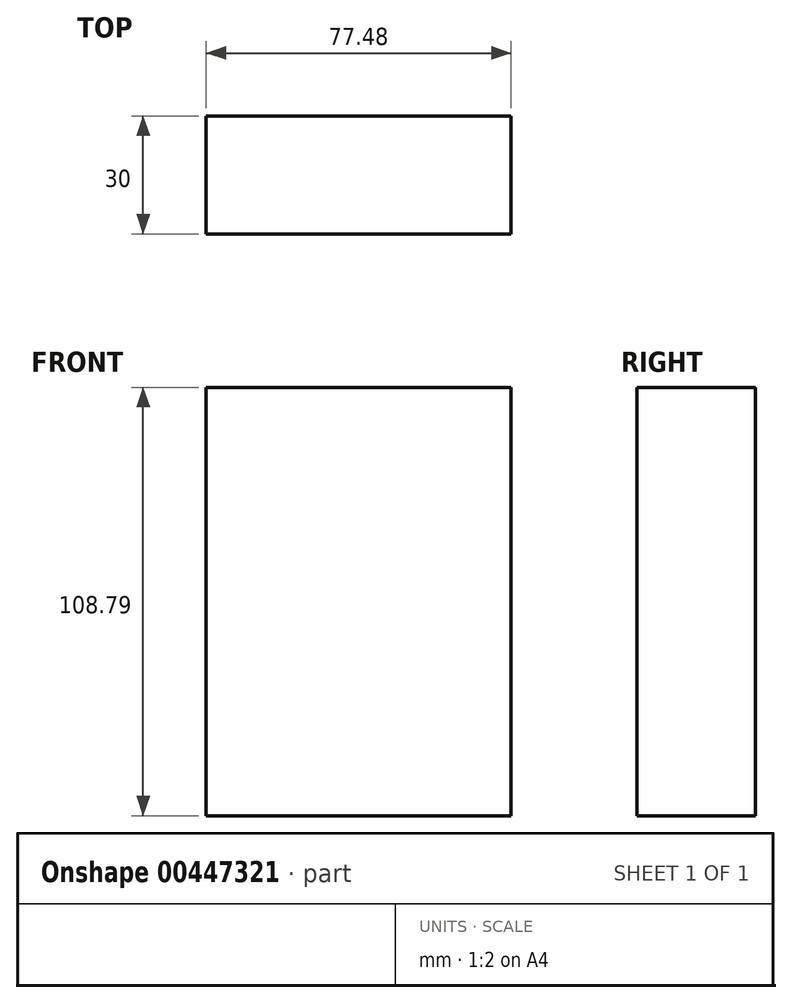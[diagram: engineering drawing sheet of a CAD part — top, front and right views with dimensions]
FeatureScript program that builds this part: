
annotation { "Feature Type Name" : "Feature", "Feature Type Description" : "" }
export const myFeature = defineFeature(function(context is Context, id is Id, definition is map)
    precondition{}
    {
        {
            var Q0;
            Q0=qCreatedBy(makeId("Front.planeOp"),FACE);
            var sketch = newSketch(context, id + "F0", { "sketchPlane" : qUnion([Q0])});
            skLineSegment(sketch, "E0.bottom", {"start": v(0, -45.02) * mm, "end": v(77.48, -45.02) * mm});
            skLineSegment(sketch, "E0.top", {"start": v(0, 63.77) * mm, "end": v(77.48, 63.77) * mm});
            skLineSegment(sketch, "E0.left", {"start": v(0, -45.02) * mm, "end": v(0, 63.77) * mm});
            skLineSegment(sketch, "E0.right", {"start": v(77.48, -45.02) * mm, "end": v(77.48, 63.77) * mm});
            skSolve(sketch);
        }
        {
            var Q0;
            Q0=makeQuery(id+"F0.imprint","IMPRINT",FACE,{"disambiguationData":[TD([[makeQuery(id+"F0.imprint","IMPRINT",EDGE,{"derivedFrom":sQuery(id+"F0.wireOp",EDGE,"E0.bottom")}),1.0]])]});
            extrude(context, id + "F1", {"entities" : qUnion([Q0]), "depth" : 30 * mm});
        }
    });
